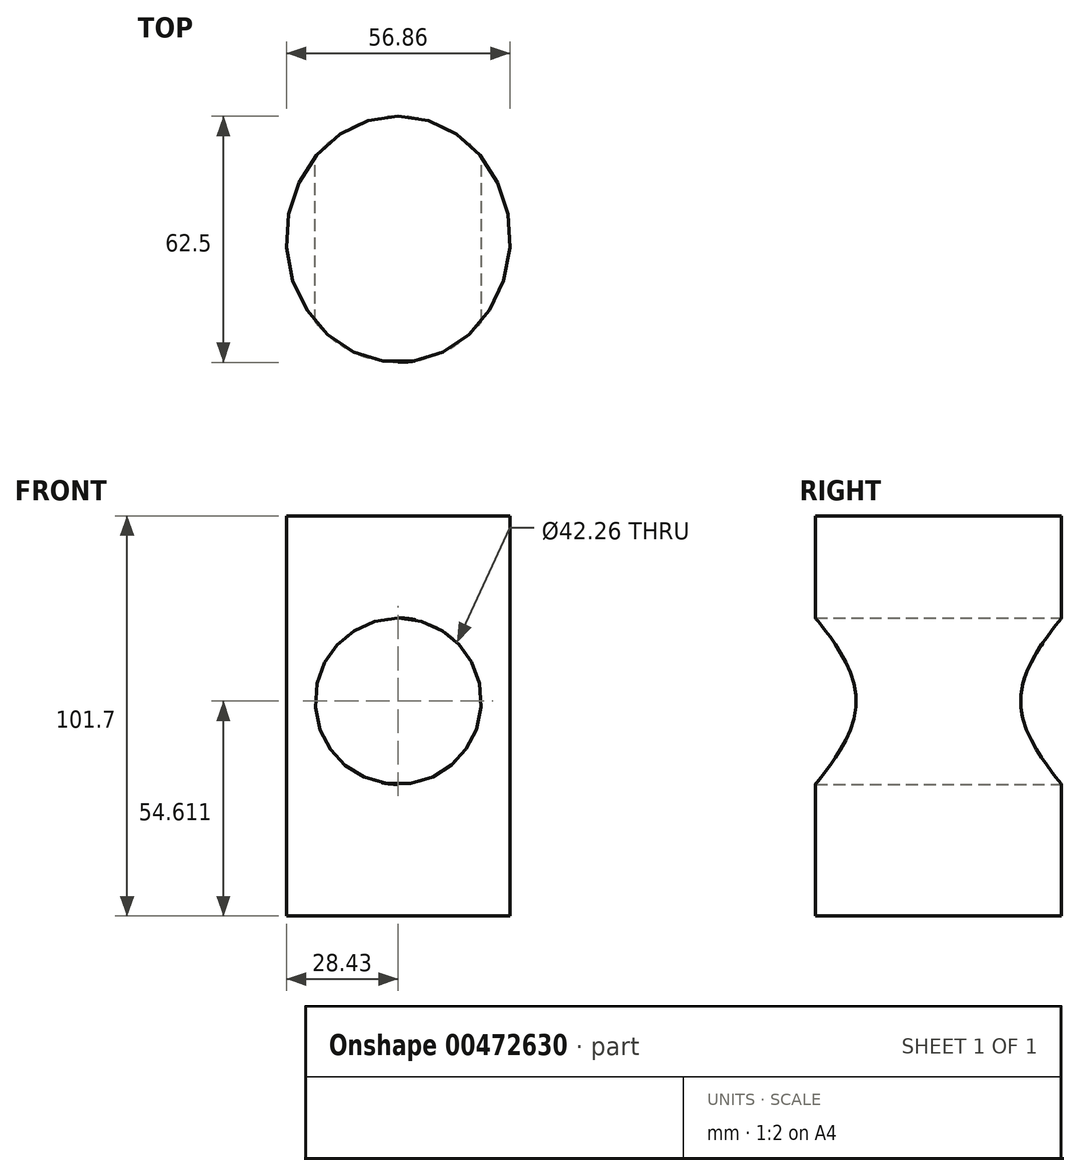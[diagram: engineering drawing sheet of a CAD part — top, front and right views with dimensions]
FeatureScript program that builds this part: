
annotation { "Feature Type Name" : "Feature", "Feature Type Description" : "" }
export const myFeature = defineFeature(function(context is Context, id is Id, definition is map)
    precondition{}
    {
        {
            var Q0;
            Q0=qCreatedBy(makeId("Front.planeOp"),FACE);
            var sketch = newSketch(context, id + "F0", { "sketchPlane" : qUnion([Q0])});
            skLineSegment(sketch, "E0.bottom", {"start": v(-29.93, 50.85) * mm, "end": v(29.93, 50.85) * mm});
            skLineSegment(sketch, "E0.top", {"start": v(-29.93, -50.85) * mm, "end": v(29.93, -50.85) * mm});
            skLineSegment(sketch, "E0.left", {"start": v(-29.93, 50.85) * mm, "end": v(-29.93, -50.85) * mm});
            skLineSegment(sketch, "E0.right", {"start": v(29.93, 50.85) * mm, "end": v(29.93, -50.85) * mm});
            skPoint(sketch, "E0.middle", {"position": v(0, 0) * mm});
            skSolve(sketch);
        }
        {
            var Q0;
            Q0 = qSketchRegion(id + "F0", true);
            extrude(context, id + "F1", {"entities" : qUnion([Q0]), "depth" : 76.2 * mm});
        }
        {
            var Q0;
            Q0=makeQuery(id+"F1.opExtrude","SWEPT_FACE",FACE,{"disambiguationData":[OSD([sQuery(id+"F0.wireOp",EDGE,"E0.top")])]});
            var sketch = newSketch(context, id + "F2", { "sketchPlane" : qUnion([Q0])});
            skEllipse(sketch, "E1", {"center": v(0, 34.66) * mm, "majorRadius": 31.25 * mm, "minorRadius": 28.43 * mm, "majorAxis": v(0, -1)});
            skSolve(sketch);
        }
        {
            var Q0;
            Q0=makeQuery(id+"F2.imprint","IMPRINT",FACE,{"disambiguationData":[TD([[makeQuery(id+"F2.imprint","IMPRINT",EDGE,{"derivedFrom":sQuery(id+"F2.wireOp",EDGE,"E1")}),-1.0]])]});
            extrude(context, id + "F3", {"entities" : qUnion([Q0]), "operationType" : NewBodyOperationType.REMOVE, "oppositeDirection" : true, "depth" : 127 * mm});
        }
        {
            var Q0;
            Q0=qCreatedBy(makeId("Front.planeOp"),FACE);
            var sketch = newSketch(context, id + "F4", { "sketchPlane" : qUnion([Q0])});
            skCircle(sketch, "E2", {"center": v(0, 3.76) * mm, "radius": 21.13 * mm});
            skSolve(sketch);
        }
        {
            var Q0;
            Q0 = qSketchRegion(id + "F4", true);
            extrude(context, id + "F5", {"entities" : qUnion([Q0]), "operationType" : NewBodyOperationType.REMOVE, "depth" : 403.86 * mm});
        }
    });
